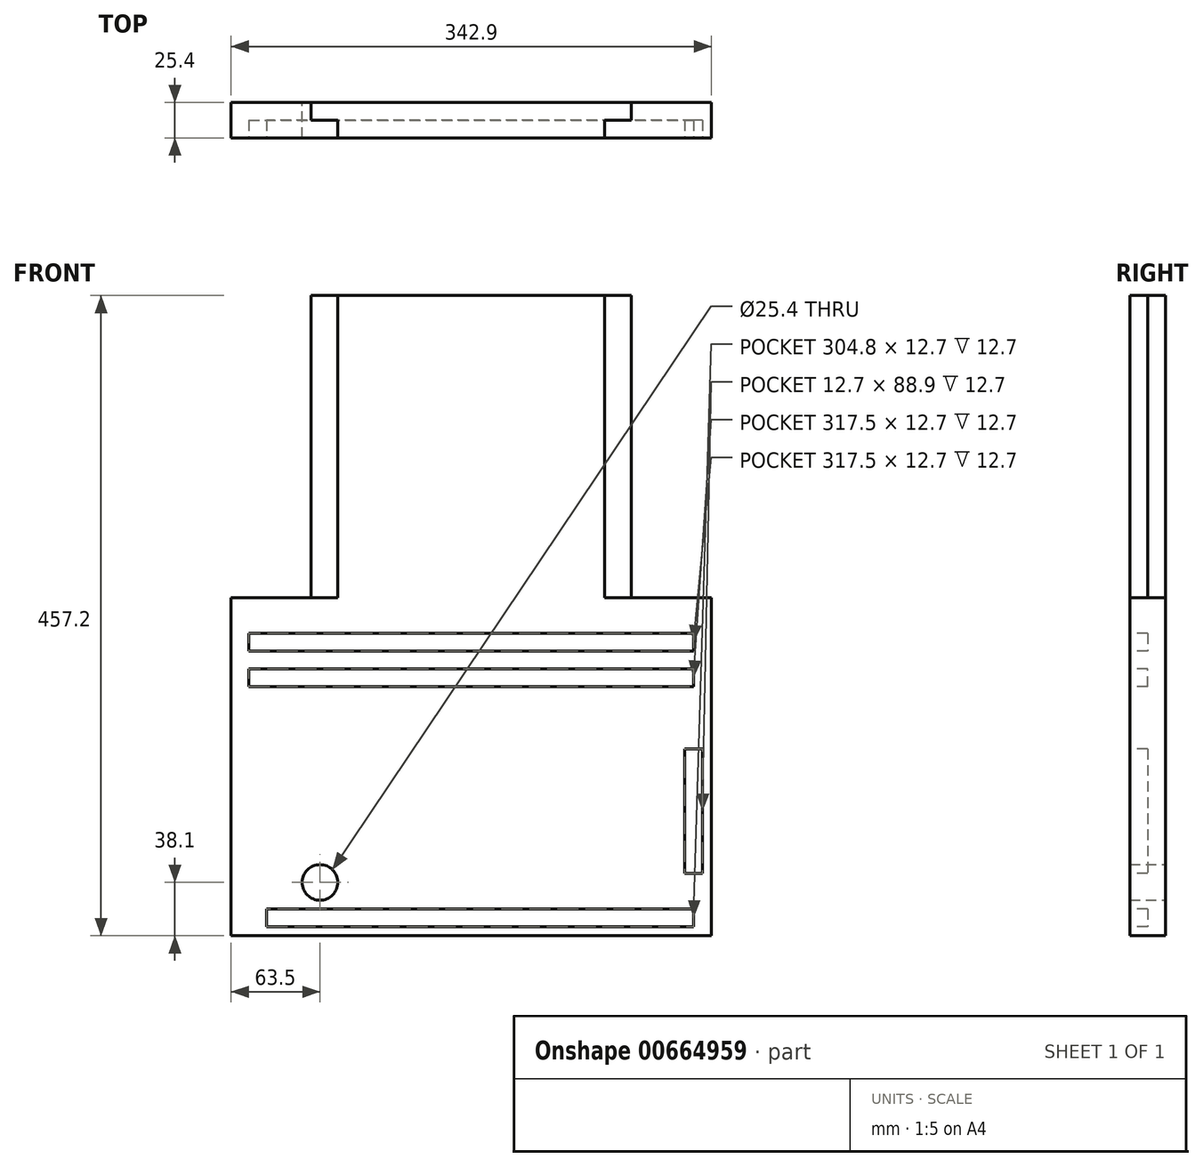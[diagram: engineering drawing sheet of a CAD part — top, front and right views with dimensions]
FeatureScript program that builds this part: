
annotation { "Feature Type Name" : "Feature", "Feature Type Description" : "" }
export const myFeature = defineFeature(function(context is Context, id is Id, definition is map)
    precondition{}
    {
        {
            var Q0;
            Q0=qCreatedBy(makeId("Front.planeOp"),FACE);
            var sketch = newSketch(context, id + "F0", { "sketchPlane" : qUnion([Q0])});
            skLineSegment(sketch, "E0.bottom", {"start": v(0, 0) * mm, "end": v(342.9, 0) * mm});
            skLineSegment(sketch, "E0.top", {"start": v(0, 177.8) * mm, "end": v(342.9, 177.8) * mm});
            skLineSegment(sketch, "E0.left", {"start": v(0, 0) * mm, "end": v(0, 177.8) * mm});
            skLineSegment(sketch, "E0.right", {"start": v(342.9, 0) * mm, "end": v(342.9, 177.8) * mm});
            skLineSegment(sketch, "E1.top", {"start": v(0, 241.3) * mm, "end": v(342.9, 241.3) * mm});
            skLineSegment(sketch, "E1.left", {"start": v(0, 177.8) * mm, "end": v(0, 241.3) * mm});
            skLineSegment(sketch, "E1.right", {"start": v(342.9, 177.8) * mm, "end": v(342.9, 241.3) * mm});
            skLineSegment(sketch, "E2", {"start": v(0, 241.3) * mm, "end": v(57.15, 241.3) * mm});
            skLineSegment(sketch, "E3.bottom", {"start": v(57.15, 241.3) * mm, "end": v(285.75, 241.3) * mm});
            skLineSegment(sketch, "E3.top", {"start": v(57.15, 457.2) * mm, "end": v(285.75, 457.2) * mm});
            skLineSegment(sketch, "E3.left", {"start": v(57.15, 241.3) * mm, "end": v(57.15, 457.2) * mm});
            skLineSegment(sketch, "E3.right", {"start": v(285.75, 241.3) * mm, "end": v(285.75, 457.2) * mm});
            skSolve(sketch);
        }
        {
            var Q0;
            Q0=makeQuery(id+"F0.imprint","IMPRINT",FACE,{"disambiguationData":[TD([[makeQuery(id+"F0.imprint","IMPRINT",EDGE,{"derivedFrom":sQuery(id+"F0.wireOp",EDGE,"E0.bottom")}),1.0]])]});
            var Q1;
            Q1=makeQuery(id+"F0.imprint","IMPRINT",FACE,{"disambiguationData":[TD([[makeQuery(id+"F0.imprint","IMPRINT",EDGE,{"derivedFrom":sQuery(id+"F0.wireOp",EDGE,"E0.top")}),1.0]])]});
            var Q2;
            Q2=makeQuery(id+"F0.imprint","IMPRINT",FACE,{"disambiguationData":[TD([[makeQuery(id+"F0.imprint","IMPRINT",EDGE,{"derivedFrom":sQuery(id+"F0.wireOp",EDGE,"E3.top")}),-1.0]])]});
            extrude(context, id + "F1", {"entities" : qUnion([Q0, Q1, Q2]), "depth" : 25.4 * mm, "offsetDistance" : 25.4 * mm});
        }
        {
            var Q0;
            Q0=makeQuery(id+"F1.opExtrude","CAP_FACE",FACE,{"disambiguationData":[OSD([sQuery(id+"F0.wireOp",EDGE,"E0.bottom"),sQuery(id+"F0.wireOp",EDGE,"E0.left"),sQuery(id+"F0.wireOp",EDGE,"E0.right"),sQuery(id+"F0.wireOp",EDGE,"E1.top"),sQuery(id+"F0.wireOp",EDGE,"E1.left"),sQuery(id+"F0.wireOp",EDGE,"E1.right"),sQuery(id+"F0.wireOp",EDGE,"E3.top"),sQuery(id+"F0.wireOp",EDGE,"E3.left"),sQuery(id+"F0.wireOp",EDGE,"E3.right")])],"isStart":false});
            var sketch = newSketch(context, id + "F2", { "sketchPlane" : qUnion([Q0])});
            skLineSegment(sketch, "E4", {"start": v(0, 0) * mm, "end": v(0, 6.35) * mm});
            skLineSegment(sketch, "E5", {"start": v(0, 6.35) * mm, "end": v(0, 19.05) * mm});
            skLineSegment(sketch, "E6", {"start": v(0, 19.05) * mm, "end": v(342.9, 19.05) * mm});
            skLineSegment(sketch, "E7", {"start": v(342.9, 19.05) * mm, "end": v(342.9, 6.35) * mm});
            skLineSegment(sketch, "E8", {"start": v(342.9, 6.35) * mm, "end": v(0, 6.35) * mm});
            skLineSegment(sketch, "E9", {"start": v(0, 19.05) * mm, "end": v(25.4, 19.05) * mm});
            skLineSegment(sketch, "E10", {"start": v(25.4, 19.05) * mm, "end": v(25.4, 6.35) * mm});
            skLineSegment(sketch, "E11", {"start": v(25.4, 6.35) * mm, "end": v(342.9, 6.35) * mm});
            skLineSegment(sketch, "E12", {"start": v(342.9, 19.05) * mm, "end": v(330.2, 19.05) * mm});
            skLineSegment(sketch, "E13", {"start": v(330.2, 19.05) * mm, "end": v(330.2, 6.35) * mm});
            skSolve(sketch);
        }
        {
            var Q0;
            {var subQ0=sQuery(id+"F2.wireOp",EDGE,"E10");Q0=makeQuery(id+"F2.imprint","IMPRINT",FACE,{"disambiguationData":[TD([[makeQuery(id+"F2.imprint","IMPRINT",EDGE,{"derivedFrom":subQ0}),1.0]])]});}
            extrude(context, id + "F3", {"entities" : qUnion([Q0]), "operationType" : NewBodyOperationType.REMOVE, "oppositeDirection" : true, "depth" : 12.7 * mm, "offsetDistance" : 25.4 * mm});
        }
        {
            var Q0;
            Q0=makeQuery(id+"F1.opExtrude","CAP_FACE",FACE,{"disambiguationData":[OSD([sQuery(id+"F0.wireOp",EDGE,"E0.bottom"),sQuery(id+"F0.wireOp",EDGE,"E0.left"),sQuery(id+"F0.wireOp",EDGE,"E0.right"),sQuery(id+"F0.wireOp",EDGE,"E1.top"),sQuery(id+"F0.wireOp",EDGE,"E1.left"),sQuery(id+"F0.wireOp",EDGE,"E1.right"),sQuery(id+"F0.wireOp",EDGE,"E3.top"),sQuery(id+"F0.wireOp",EDGE,"E3.left"),sQuery(id+"F0.wireOp",EDGE,"E3.right")])],"isStart":false});
            var sketch = newSketch(context, id + "F4", { "sketchPlane" : qUnion([Q0])});
            skLineSegment(sketch, "E14", {"start": v(0, 0) * mm, "end": v(0, -6.35) * mm});
            skLineSegment(sketch, "E15", {"start": v(0, -6.35) * mm, "end": v(0, -19.05) * mm});
            skLineSegment(sketch, "E16", {"start": v(0, -19.05) * mm, "end": v(342.9, -19.05) * mm});
            skLineSegment(sketch, "E17", {"start": v(342.9, -19.05) * mm, "end": v(342.9, -6.35) * mm});
            skLineSegment(sketch, "E18", {"start": v(342.9, -6.35) * mm, "end": v(0, -6.35) * mm});
            skLineSegment(sketch, "E19", {"start": v(0, -19.05) * mm, "end": v(25.4, -19.05) * mm});
            skLineSegment(sketch, "E20", {"start": v(25.4, -19.05) * mm, "end": v(25.4, -6.35) * mm});
            skLineSegment(sketch, "E21", {"start": v(25.4, -6.35) * mm, "end": v(342.9, -6.35) * mm});
            skLineSegment(sketch, "E22", {"start": v(342.9, -6.35) * mm, "end": v(330.2, -6.35) * mm});
            skLineSegment(sketch, "E23", {"start": v(330.2, -6.35) * mm, "end": v(330.2, -19.05) * mm});
            skSolve(sketch);
        }
        {
            var Q0;
            {var subQ0=sQuery(id+"F4.wireOp",EDGE,"E20");Q0=makeQuery(id+"F4.imprint","IMPRINT",FACE,{"disambiguationData":[TD([[makeQuery(id+"F4.imprint","IMPRINT",EDGE,{"derivedFrom":subQ0}),-1.0]])]});}
            extrude(context, id + "F5", {"entities" : qUnion([Q0]), "operationType" : NewBodyOperationType.REMOVE, "oppositeDirection" : true, "depth" : 12.7 * mm, "offsetDistance" : 25.4 * mm});
        }
        {
            var Q0;
            Q0=makeQuery(id+"F1.opExtrude","CAP_FACE",FACE,{"disambiguationData":[OSD([sQuery(id+"F0.wireOp",EDGE,"E0.bottom"),sQuery(id+"F0.wireOp",EDGE,"E0.left"),sQuery(id+"F0.wireOp",EDGE,"E0.right"),sQuery(id+"F0.wireOp",EDGE,"E1.top"),sQuery(id+"F0.wireOp",EDGE,"E1.left"),sQuery(id+"F0.wireOp",EDGE,"E1.right"),sQuery(id+"F0.wireOp",EDGE,"E3.top"),sQuery(id+"F0.wireOp",EDGE,"E3.left"),sQuery(id+"F0.wireOp",EDGE,"E3.right")])],"isStart":true});
            var sketch = newSketch(context, id + "F6", { "sketchPlane" : qUnion([Q0])});
            skCircle(sketch, "E24", {"center": v(-63.5, 38.1) * mm, "radius": 12.7 * mm});
            skSolve(sketch);
        }
        {
            var Q0;
            Q0=makeQuery(id+"F6.imprint","IMPRINT",FACE,{"disambiguationData":[TD([[makeQuery(id+"F6.imprint","IMPRINT",EDGE,{"derivedFrom":sQuery(id+"F6.wireOp",EDGE,"E24")}),1.0]])]});
            extrude(context, id + "F7", {"entities" : qUnion([Q0]), "operationType" : NewBodyOperationType.REMOVE, "oppositeDirection" : true, "depth" : 25.4 * mm, "offsetDistance" : 25.4 * mm});
        }
        {
            var Q0;
            Q0=makeQuery(id+"F1.opExtrude","CAP_FACE",FACE,{"disambiguationData":[OSD([sQuery(id+"F0.wireOp",EDGE,"E0.bottom"),sQuery(id+"F0.wireOp",EDGE,"E0.left"),sQuery(id+"F0.wireOp",EDGE,"E0.right"),sQuery(id+"F0.wireOp",EDGE,"E1.top"),sQuery(id+"F0.wireOp",EDGE,"E1.left"),sQuery(id+"F0.wireOp",EDGE,"E1.right"),sQuery(id+"F0.wireOp",EDGE,"E3.top"),sQuery(id+"F0.wireOp",EDGE,"E3.left"),sQuery(id+"F0.wireOp",EDGE,"E3.right")])],"isStart":false});
            var sketch = newSketch(context, id + "F8", { "sketchPlane" : qUnion([Q0])});
            skLineSegment(sketch, "E25", {"start": v(330.2, 19.05) * mm, "end": v(330.2, 44.45) * mm});
            skLineSegment(sketch, "E26", {"start": v(330.2, 44.45) * mm, "end": v(323.85, 44.45) * mm});
            skLineSegment(sketch, "E27.bottom", {"start": v(336.55, 133.35) * mm, "end": v(323.85, 133.35) * mm});
            skLineSegment(sketch, "E27.top", {"start": v(336.55, 44.45) * mm, "end": v(323.85, 44.45) * mm});
            skLineSegment(sketch, "E27.left", {"start": v(336.55, 133.35) * mm, "end": v(336.55, 44.45) * mm});
            skLineSegment(sketch, "E27.right", {"start": v(323.85, 133.35) * mm, "end": v(323.85, 44.45) * mm});
            skSolve(sketch);
        }
        {
            var Q0;
            Q0=makeQuery(id+"F8.imprint","IMPRINT",FACE,{"disambiguationData":[TD([[makeQuery(id+"F8.imprint","IMPRINT",EDGE,{"derivedFrom":sQuery(id+"F8.wireOp",EDGE,"E26")}),-1.0]])]});
            extrude(context, id + "F9", {"entities" : qUnion([Q0]), "operationType" : NewBodyOperationType.REMOVE, "oppositeDirection" : true, "depth" : 12.7 * mm, "offsetDistance" : 25.4 * mm});
        }
        {
            var Q0;
            Q0=makeQuery(id+"F1.opExtrude","CAP_FACE",FACE,{"disambiguationData":[OSD([sQuery(id+"F0.wireOp",EDGE,"E0.bottom"),sQuery(id+"F0.wireOp",EDGE,"E0.left"),sQuery(id+"F0.wireOp",EDGE,"E0.right"),sQuery(id+"F0.wireOp",EDGE,"E1.top"),sQuery(id+"F0.wireOp",EDGE,"E1.left"),sQuery(id+"F0.wireOp",EDGE,"E1.right"),sQuery(id+"F0.wireOp",EDGE,"E3.top"),sQuery(id+"F0.wireOp",EDGE,"E3.left"),sQuery(id+"F0.wireOp",EDGE,"E3.right")])],"isStart":false});
            var sketch = newSketch(context, id + "F10", { "sketchPlane" : qUnion([Q0])});
            skLineSegment(sketch, "E28.bottom", {"start": v(285.75, 457.2) * mm, "end": v(266.7, 457.2) * mm});
            skLineSegment(sketch, "E28.top", {"start": v(285.75, 241.3) * mm, "end": v(266.7, 241.3) * mm});
            skLineSegment(sketch, "E28.left", {"start": v(285.75, 457.2) * mm, "end": v(285.75, 241.3) * mm});
            skLineSegment(sketch, "E28.right", {"start": v(266.7, 457.2) * mm, "end": v(266.7, 241.3) * mm});
            skLineSegment(sketch, "E29.bottom", {"start": v(57.15, 457.2) * mm, "end": v(76.2, 457.2) * mm});
            skLineSegment(sketch, "E29.top", {"start": v(57.15, 241.3) * mm, "end": v(76.2, 241.3) * mm});
            skLineSegment(sketch, "E29.left", {"start": v(57.15, 457.2) * mm, "end": v(57.15, 241.3) * mm});
            skLineSegment(sketch, "E29.right", {"start": v(76.2, 457.2) * mm, "end": v(76.2, 241.3) * mm});
            skLineSegment(sketch, "E30.bottom", {"start": v(76.2, 457.2) * mm, "end": v(266.7, 457.2) * mm});
            skLineSegment(sketch, "E30.top", {"start": v(76.2, 438.15) * mm, "end": v(266.7, 438.15) * mm});
            skLineSegment(sketch, "E30.left", {"start": v(76.2, 457.2) * mm, "end": v(76.2, 438.15) * mm});
            skLineSegment(sketch, "E30.right", {"start": v(266.7, 457.2) * mm, "end": v(266.7, 438.15) * mm});
            skSolve(sketch);
        }
        {
            var Q0;
            {var subQ3=sQuery(id+"F10.wireOp",EDGE,"E29.bottom");Q0=makeQuery(id+"F10.imprint","IMPRINT",FACE,{"disambiguationData":[TD([[makeQuery(id+"F10.imprint","IMPRINT",EDGE,{"derivedFrom":subQ3}),-1.0]])]});}
            var Q1;
            {var subQ3=sQuery(id+"F10.wireOp",EDGE,"E28.bottom");Q1=makeQuery(id+"F10.imprint","IMPRINT",FACE,{"disambiguationData":[TD([[makeQuery(id+"F10.imprint","IMPRINT",EDGE,{"derivedFrom":subQ3}),-1.0]])]});}
            extrude(context, id + "F11", {"entities" : qUnion([Q0, Q1]), "operationType" : NewBodyOperationType.REMOVE, "oppositeDirection" : true, "depth" : 12.7 * mm, "offsetDistance" : 25.4 * mm});
        }
        {
            var Q0;
            Q0=makeQuery(id+"F1.opExtrude","CAP_FACE",FACE,{"disambiguationData":[OSD([sQuery(id+"F0.wireOp",EDGE,"E0.bottom"),sQuery(id+"F0.wireOp",EDGE,"E0.left"),sQuery(id+"F0.wireOp",EDGE,"E0.right"),sQuery(id+"F0.wireOp",EDGE,"E1.top"),sQuery(id+"F0.wireOp",EDGE,"E1.left"),sQuery(id+"F0.wireOp",EDGE,"E1.right"),sQuery(id+"F0.wireOp",EDGE,"E3.top"),sQuery(id+"F0.wireOp",EDGE,"E3.left"),sQuery(id+"F0.wireOp",EDGE,"E3.right")])],"isStart":false});
            var sketch = newSketch(context, id + "F12", { "sketchPlane" : qUnion([Q0])});
            skLineSegment(sketch, "E31", {"start": v(0, 241.3) * mm, "end": v(0, 215.9) * mm});
            skLineSegment(sketch, "E32", {"start": v(0, 215.9) * mm, "end": v(12.7, 215.9) * mm});
            skLineSegment(sketch, "E33", {"start": v(12.7, 215.9) * mm, "end": v(330.2, 215.9) * mm});
            skLineSegment(sketch, "E34", {"start": v(330.2, 215.9) * mm, "end": v(330.2, 203.2) * mm});
            skLineSegment(sketch, "E35", {"start": v(330.2, 203.2) * mm, "end": v(12.7, 203.2) * mm});
            skLineSegment(sketch, "E36", {"start": v(12.7, 203.2) * mm, "end": v(12.7, 215.9) * mm});
            skLineSegment(sketch, "E37", {"start": v(12.7, 203.2) * mm, "end": v(12.7, 190.5) * mm});
            skLineSegment(sketch, "E38", {"start": v(12.7, 190.5) * mm, "end": v(330.2, 190.5) * mm});
            skLineSegment(sketch, "E39", {"start": v(330.2, 190.5) * mm, "end": v(330.2, 177.8) * mm});
            skLineSegment(sketch, "E40", {"start": v(330.2, 177.8) * mm, "end": v(12.7, 177.8) * mm});
            skLineSegment(sketch, "E41", {"start": v(12.7, 177.8) * mm, "end": v(12.7, 190.5) * mm});
            skSolve(sketch);
        }
        {
            var Q0;
            Q0=makeQuery(id+"F12.imprint","IMPRINT",FACE,{"disambiguationData":[TD([[makeQuery(id+"F12.imprint","IMPRINT",EDGE,{"derivedFrom":sQuery(id+"F12.wireOp",EDGE,"E33")}),-1.0]])]});
            var Q1;
            Q1=makeQuery(id+"F12.imprint","IMPRINT",FACE,{"disambiguationData":[TD([[makeQuery(id+"F12.imprint","IMPRINT",EDGE,{"derivedFrom":sQuery(id+"F12.wireOp",EDGE,"E38")}),-1.0]])]});
            extrude(context, id + "F13", {"entities" : qUnion([Q0, Q1]), "operationType" : NewBodyOperationType.REMOVE, "oppositeDirection" : true, "depth" : 12.7 * mm, "offsetDistance" : 25.4 * mm});
        }
    });
